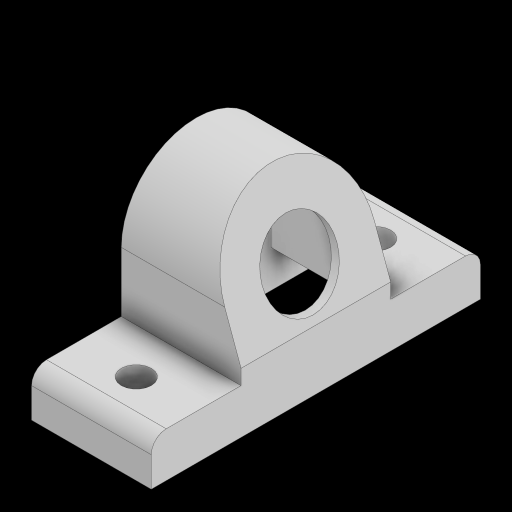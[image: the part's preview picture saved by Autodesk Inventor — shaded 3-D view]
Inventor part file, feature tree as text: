
AUTODESK INVENTOR PART (.ipt)
format: ipt  version: 2024 (Build 280153000, 153)  size: 194,560 bytes
history: native  units: in
note: dims shown in document units (in); Inventor stores cm internally (conversion verified against a paired STEP export)
features: sketch x5, extrude x4, hole x1, mirror x1, fillet x1, shell x1
ambient origin geometry x8: Origin, YZ Plane, XZ Plane, XY Plane, X Axis, Y Axis, Z Axis, Center Point
bodies: Solid1 (feature_tree)
feature tree (13):
  extrude  "BASE"  Depth=4.0in
  extrude  "ARCH"  Depth=5.0in
  extrude  "ANGLED CUT"  TaperAngle=0.0deg  [1 undecoded]
  hole  "Hole1"  [1 undecoded]
  mirror  "Mirror1"
  fillet  "Fillet1"  Radius=0.1374in
  shell  "Shell1"  Thickness=0.0in
  extrude  "Extrusion4"  Depth=4.0in
  sketch  "Sketch1"  dims[d0=11.0in d1=4.0in]
  sketch  "Sketch2"  dims[d2=1.5in d3=0.0in d4=5.0in]
  sketch  "Sketch3"  dims[d5=3.5in d7=0.0in]
  sketch  "Sketch4"  dims[d8=4.0in d9=0.0in d11=2.0in d12=0.1374in d13=0.0in d14=0.0in]
  sketch  "Sketch5"  dims[d15=1.0in d16=0.75in d17=0.375in d18=0.25in d19=0.5635in d20=1.0in d21=0.8108in d22=4.0in d23=2.0in d24=0.5in d25=0.25in d26=2.5in d27=3.5in d28=0.0in d29=1.0in d30=0.0in d31=0.5in d32=0.0344in]
note: 2 required parameter values undecoded (feature->parameter linkage not recoverable at this tier; creation-order binding heuristic only, values carry confidence <= 0.55)
